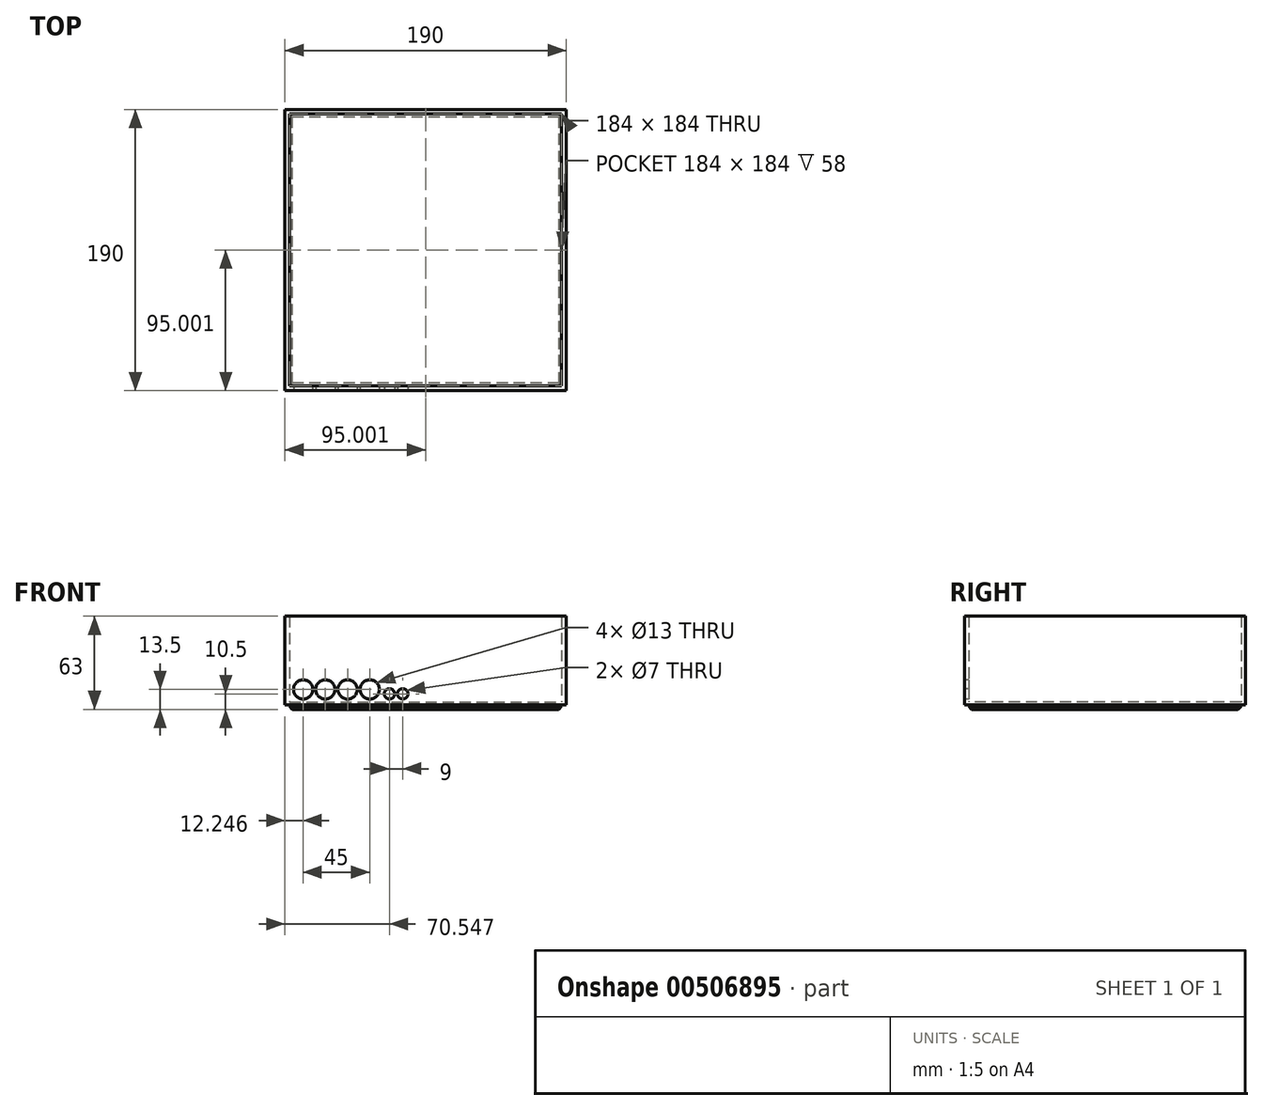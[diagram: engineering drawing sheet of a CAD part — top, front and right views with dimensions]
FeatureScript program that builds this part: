
annotation { "Feature Type Name" : "Feature", "Feature Type Description" : "" }
export const myFeature = defineFeature(function(context is Context, id is Id, definition is map)
    precondition{}
    {
        {
            var Q0;
            Q0=qCreatedBy(makeId("Top.planeOp"),FACE);
            var sketch = newSketch(context, id + "F0", { "sketchPlane" : qUnion([Q0])});
            skLineSegment(sketch, "E0.bottom", {"start": v(-59.37, 136.02) * mm, "end": v(130.63, 136.02) * mm});
            skLineSegment(sketch, "E0.top", {"start": v(-59.37, -53.98) * mm, "end": v(130.63, -53.98) * mm});
            skLineSegment(sketch, "E0.left", {"start": v(-59.37, 136.02) * mm, "end": v(-59.37, -53.98) * mm});
            skLineSegment(sketch, "E0.right", {"start": v(130.63, 136.02) * mm, "end": v(130.63, -53.98) * mm});
            skLineSegment(sketch, "E1.bottom", {"start": v(-56.37, 133.02) * mm, "end": v(127.63, 133.02) * mm});
            skLineSegment(sketch, "E1.top", {"start": v(-56.37, -50.98) * mm, "end": v(127.63, -50.98) * mm});
            skLineSegment(sketch, "E1.left", {"start": v(-56.37, 133.02) * mm, "end": v(-56.37, -50.98) * mm});
            skLineSegment(sketch, "E1.right", {"start": v(127.63, 133.02) * mm, "end": v(127.63, -50.98) * mm});
            skSolve(sketch);
        }
        {
            var Q0;
            Q0=makeQuery(id+"F0.imprint","IMPRINT",FACE,{"disambiguationData":[TD([[makeQuery(id+"F0.imprint","IMPRINT",EDGE,{"derivedFrom":sQuery(id+"F0.wireOp",EDGE,"E1.bottom")}),-1.0]])]});
            var Q1;
            Q1 = qSketchRegion(id + "F3", true);
            extrude(context, id + "F1", {"entities" : qUnion([Q0, Q1]), "depth" : 2 * mm});
        }
        {
            var Q0;
            Q0 = qSketchRegion(id + "F0", true);
            extrude(context, id + "F2", {"entities" : qUnion([Q0]), "operationType" : NewBodyOperationType.ADD, "depth" : 60 * mm});
        }
        {
            var Q0;
            Q0=makeQuery(id+"F2.opExtrude","SWEPT_FACE",FACE,{"disambiguationData":[OSD([sQuery(id+"F0.wireOp",EDGE,"E0.top")])]});
            var sketch = newSketch(context, id + "F3", { "sketchPlane" : qUnion([Q0])});
            skCircle(sketch, "E2", {"center": v(-47.12, 10.5) * mm, "radius": 6.5 * mm});
            skCircle(sketch, "E3", {"center": v(-32.12, 10.5) * mm, "radius": 6.5 * mm});
            skCircle(sketch, "E4", {"center": v(11.18, 7.5) * mm, "radius": 3.5 * mm});
            skCircle(sketch, "E5", {"center": v(20.18, 7.5) * mm, "radius": 3.5 * mm});
            skCircle(sketch, "E6", {"center": v(-17.12, 10.5) * mm, "radius": 6.5 * mm});
            skCircle(sketch, "E7", {"center": v(-2.12, 10.5) * mm, "radius": 6.5 * mm});
            skSolve(sketch);
        }
        {
            var Q0;
            Q0=makeQuery(id+"F3.imprint","IMPRINT",FACE,{"disambiguationData":[TD([[makeQuery(id+"F3.imprint","IMPRINT",EDGE,{"derivedFrom":sQuery(id+"F3.wireOp",EDGE,"E5")}),1.0]])]});
            var Q1;
            Q1=makeQuery(id+"F3.imprint","IMPRINT",FACE,{"disambiguationData":[TD([[makeQuery(id+"F3.imprint","IMPRINT",EDGE,{"derivedFrom":sQuery(id+"F3.wireOp",EDGE,"E4")}),1.0]])]});
            var Q2;
            Q2=makeQuery(id+"F3.imprint","IMPRINT",FACE,{"disambiguationData":[TD([[makeQuery(id+"F3.imprint","IMPRINT",EDGE,{"derivedFrom":sQuery(id+"F3.wireOp",EDGE,"E3")}),1.0]])]});
            var Q3;
            Q3=makeQuery(id+"F3.imprint","IMPRINT",FACE,{"disambiguationData":[TD([[makeQuery(id+"F3.imprint","IMPRINT",EDGE,{"derivedFrom":sQuery(id+"F3.wireOp",EDGE,"E2")}),1.0]])]});
            var Q4;
            Q4=makeQuery(id+"F3.imprint","IMPRINT",FACE,{"disambiguationData":[TD([[makeQuery(id+"F3.imprint","IMPRINT",EDGE,{"derivedFrom":sQuery(id+"F3.wireOp",EDGE,"E6")}),1.0]])]});
            var Q5;
            Q5=makeQuery(id+"F3.imprint","IMPRINT",FACE,{"disambiguationData":[TD([[makeQuery(id+"F3.imprint","IMPRINT",EDGE,{"derivedFrom":sQuery(id+"F3.wireOp",EDGE,"E7")}),1.0]])]});
            extrude(context, id + "F4", {"entities" : qUnion([Q0, Q1, Q2, Q3, Q4, Q5]), "operationType" : NewBodyOperationType.REMOVE, "oppositeDirection" : true, "depth" : 4 * mm});
        }
        {
            var Q0;
            Q0=makeQuery(id+"F0.imprint","IMPRINT",FACE,{"disambiguationData":[TD([[makeQuery(id+"F0.imprint","IMPRINT",EDGE,{"derivedFrom":sQuery(id+"F0.wireOp",EDGE,"E1.bottom")}),-1.0]])]});
            extrude(context, id + "F5", {"entities" : qUnion([Q0]), "operationType" : NewBodyOperationType.ADD, "oppositeDirection" : true, "depth" : 3 * mm});
        }
        {
            var Q0;
            Q0=makeQuery(id+"F5.opExtrude","CAP_FACE",FACE,{"disambiguationData":[OSD([sQuery(id+"F0.wireOp",EDGE,"E1.bottom"),sQuery(id+"F0.wireOp",EDGE,"E1.top"),sQuery(id+"F0.wireOp",EDGE,"E1.left"),sQuery(id+"F0.wireOp",EDGE,"E1.right")])],"isStart":false});
            chamfer(context, id + "F6", {"entities" : qUnion([Q0]), "width" : 2 * mm, "tangentPropagation" : true});
        }
    });
